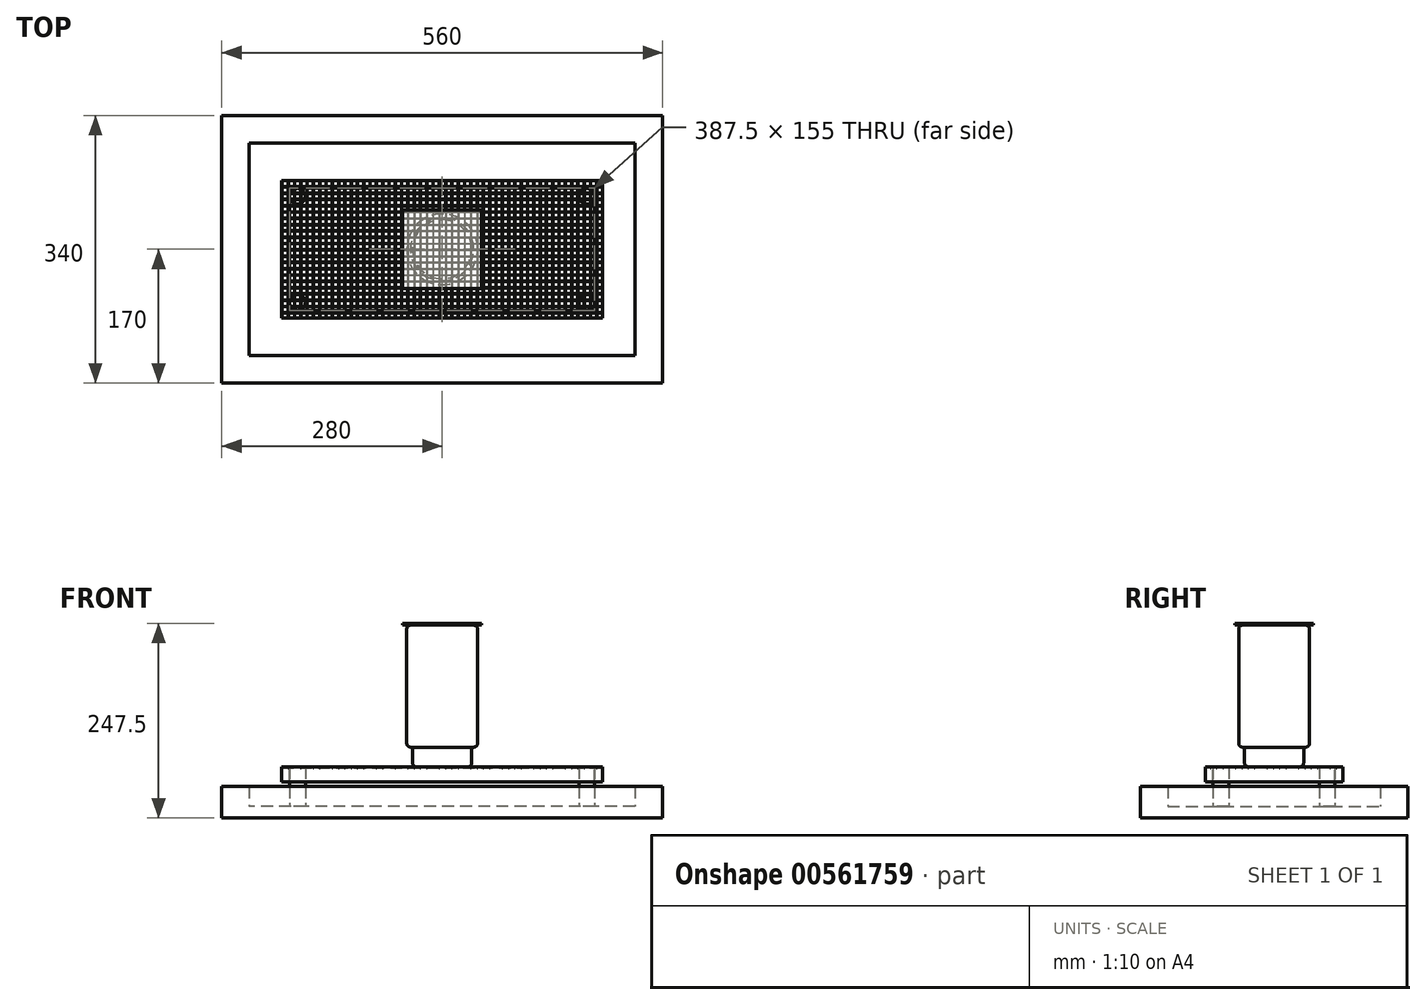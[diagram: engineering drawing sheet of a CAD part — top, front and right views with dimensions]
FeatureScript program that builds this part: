
annotation { "Feature Type Name" : "Feature", "Feature Type Description" : "" }
export const myFeature = defineFeature(function(context is Context, id is Id, definition is map)
    precondition{}
    {
        {
            var Q0;
            Q0=qCreatedBy(makeId("Top.planeOp"),FACE);
            cPlane(context, id + "F0", {"entities" : qUnion([Q0]), "cplaneType" : CPlaneType.OFFSET, "offset" : 167.5 * mm, "oppositeDirection" : true, "width" : 150 * mm, "height" : 150 * mm});
        }
        {
            var Q0;
            Q0=qCreatedBy(id+"F0.planeOp",FACE);
            var sketch = newSketch(context, id + "F1", { "sketchPlane" : qUnion([Q0])});
            skLineSegment(sketch, "E0.bottom", {"start": v(280, -170) * mm, "end": v(-280, -170) * mm});
            skLineSegment(sketch, "E0.top", {"start": v(280, 170) * mm, "end": v(-280, 170) * mm});
            skLineSegment(sketch, "E0.left", {"start": v(280, -170) * mm, "end": v(280, 170) * mm});
            skLineSegment(sketch, "E0.right", {"start": v(-280, -170) * mm, "end": v(-280, 170) * mm});
            skPoint(sketch, "E0.middle", {"position": v(0, 0) * mm});
            skSolve(sketch);
        }
        {
            var Q0;
            Q0=makeQuery(id+"F1.imprint","IMPRINT",FACE,{"disambiguationData":[TD([[makeQuery(id+"F1.imprint","IMPRINT",EDGE,{"derivedFrom":sQuery(id+"F1.wireOp",EDGE,"E0.bottom")}),-1.0]])]});
            extrude(context, id + "F2", {"entities" : qUnion([Q0]), "depth" : 40 * mm, "offsetDistance" : 25 * mm});
        }
        {
            var Q0;
            Q0=makeQuery(id+"F2.opExtrude","CAP_FACE",FACE,{"disambiguationData":[OSD([sQuery(id+"F1.wireOp",EDGE,"E0.bottom"),sQuery(id+"F1.wireOp",EDGE,"E0.top"),sQuery(id+"F1.wireOp",EDGE,"E0.left"),sQuery(id+"F1.wireOp",EDGE,"E0.right")])],"isStart":false});
            shell(context, id + "F3", {"entities" : qUnion([Q0]), "thickness" : 35 * mm});
        }
        {
            var Q0;
            Q0=makeQuery(id+"F3.opShell","OFFSET_FACE",FACE,{"disambiguationData":[OSD([sQuery(id+"F1.wireOp",EDGE,"E0.bottom"),sQuery(id+"F1.wireOp",EDGE,"E0.top"),sQuery(id+"F1.wireOp",EDGE,"E0.left"),sQuery(id+"F1.wireOp",EDGE,"E0.right")])]});
            var sketch = newSketch(context, id + "F4", { "sketchPlane" : qUnion([Q0])});
            skLineSegment(sketch, "E1.bottom", {"start": v(245, 135) * mm, "end": v(-245, 135) * mm});
            skLineSegment(sketch, "E1.top", {"start": v(245, -135) * mm, "end": v(-245, -135) * mm});
            skLineSegment(sketch, "E1.left", {"start": v(245, 135) * mm, "end": v(245, -135) * mm});
            skLineSegment(sketch, "E1.right", {"start": v(-245, 135) * mm, "end": v(-245, -135) * mm});
            skPoint(sketch, "E1.middle", {"position": v(0, 0) * mm});
            skSolve(sketch);
        }
        {
            var Q0;
            Q0=makeQuery(id+"F4.imprint","IMPRINT",FACE,{"disambiguationData":[TD([[makeQuery(id+"F4.imprint","IMPRINT",EDGE,{"derivedFrom":sQuery(id+"F4.wireOp",EDGE,"E1.bottom")}),1.0]])]});
            extrude(context, id + "F5", {"entities" : qUnion([Q0]), "operationType" : NewBodyOperationType.REMOVE, "oppositeDirection" : true, "depth" : 20 * mm, "offsetDistance" : 25 * mm});
        }
        {
            var Q0;
            Q0=makeQuery(id+"F5.boolean.opBoolean","COPY",FACE,{"derivedFrom":makeQuery(id+"F5.opExtrude","CAP_FACE",FACE,{"disambiguationData":[OSD([sQuery(id+"F4.wireOp",EDGE,"E1.bottom"),sQuery(id+"F4.wireOp",EDGE,"E1.top"),sQuery(id+"F4.wireOp",EDGE,"E1.left"),sQuery(id+"F4.wireOp",EDGE,"E1.right")])],"isStart":false})});
            var sketch = newSketch(context, id + "F6", { "sketchPlane" : qUnion([Q0])});
            skCircle(sketch, "E2", {"center": v(-183.75, 67.5) * mm, "radius": 10 * mm});
            skCircle(sketch, "E3", {"center": v(-183.75, -67.5) * mm, "radius": 10 * mm});
            skCircle(sketch, "E4", {"center": v(183.75, -67.5) * mm, "radius": 10 * mm});
            skCircle(sketch, "E5", {"center": v(183.75, 67.5) * mm, "radius": 10 * mm});
            skSolve(sketch);
        }
        {
            var Q0;
            Q0=makeQuery(id+"F6.imprint","IMPRINT",FACE,{"disambiguationData":[TD([[makeQuery(id+"F6.imprint","IMPRINT",EDGE,{"derivedFrom":sQuery(id+"F6.wireOp",EDGE,"E2")}),1.0]])]});
            var Q1;
            Q1=makeQuery(id+"F6.imprint","IMPRINT",FACE,{"disambiguationData":[TD([[makeQuery(id+"F6.imprint","IMPRINT",EDGE,{"derivedFrom":sQuery(id+"F6.wireOp",EDGE,"E5")}),1.0]])]});
            var Q2;
            Q2=makeQuery(id+"F6.imprint","IMPRINT",FACE,{"disambiguationData":[TD([[makeQuery(id+"F6.imprint","IMPRINT",EDGE,{"derivedFrom":sQuery(id+"F6.wireOp",EDGE,"E3")}),1.0]])]});
            var Q3;
            Q3=makeQuery(id+"F6.imprint","IMPRINT",FACE,{"disambiguationData":[TD([[makeQuery(id+"F6.imprint","IMPRINT",EDGE,{"derivedFrom":sQuery(id+"F6.wireOp",EDGE,"E4")}),1.0]])]});
            extrude(context, id + "F7", {"entities" : qUnion([Q0, Q1, Q2, Q3]), "operationType" : NewBodyOperationType.ADD, "depth" : 50 * mm, "offsetDistance" : 25 * mm});
        }
        {
            var Q0;
            Q0=makeQuery(id+"F7.opExtrude","CAP_FACE",FACE,{"disambiguationData":[OSD([sQuery(id+"F6.wireOp",EDGE,"E2")])],"isStart":false});
            var sketch = newSketch(context, id + "F8", { "sketchPlane" : qUnion([Q0])});
            skLineSegment(sketch, "E6.bottom", {"start": v(-183.75, 67.5) * mm, "end": v(183.75, 67.5) * mm});
            skLineSegment(sketch, "E6.top", {"start": v(-183.75, -67.5) * mm, "end": v(183.75, -67.5) * mm});
            skLineSegment(sketch, "E6.left", {"start": v(-183.75, 67.5) * mm, "end": v(-183.75, -67.5) * mm});
            skLineSegment(sketch, "E6.right", {"start": v(183.75, 67.5) * mm, "end": v(183.75, -67.5) * mm});
            skPoint(sketch, "E6.middle", {"position": v(0, 0) * mm});
            skLineSegment(sketch, "E7.bottom", {"start": v(193.75, 77.5) * mm, "end": v(-193.75, 77.5) * mm});
            skLineSegment(sketch, "E7.top", {"start": v(193.75, -77.5) * mm, "end": v(-193.75, -77.5) * mm});
            skLineSegment(sketch, "E7.left", {"start": v(193.75, 77.5) * mm, "end": v(193.75, -77.5) * mm});
            skLineSegment(sketch, "E7.right", {"start": v(-193.75, 77.5) * mm, "end": v(-193.75, -77.5) * mm});
            skLineSegment(sketch, "E8.bottom", {"start": v(203.75, 87.5) * mm, "end": v(-203.75, 87.5) * mm});
            skLineSegment(sketch, "E8.top", {"start": v(203.75, -87.5) * mm, "end": v(-203.75, -87.5) * mm});
            skLineSegment(sketch, "E8.left", {"start": v(203.75, 87.5) * mm, "end": v(203.75, -87.5) * mm});
            skLineSegment(sketch, "E8.right", {"start": v(-203.75, 87.5) * mm, "end": v(-203.75, -87.5) * mm});
            skSolve(sketch);
        }
        {
            var Q0;
            {var subQ1=sQuery(id+"F8.wireOp",EDGE,"E7.top");Q0=makeQuery(id+"F8.imprint","IMPRINT",FACE,{"disambiguationData":[TD([[makeQuery(id+"F8.imprint","IMPRINT",EDGE,{"derivedFrom":subQ1}),1.0]])]});}
            extrude(context, id + "F9", {"entities" : qUnion([Q0]), "operationType" : NewBodyOperationType.ADD, "oppositeDirection" : true, "depth" : 19.05 * mm, "offsetDistance" : 25 * mm});
        }
        {
            var Q0;
            Q0=makeQuery(id+"F9.opExtrude","CAP_FACE",FACE,{"disambiguationData":[OSD([sQuery(id+"F8.wireOp",EDGE,"E7.bottom"),sQuery(id+"F8.wireOp",EDGE,"E7.top"),sQuery(id+"F8.wireOp",EDGE,"E7.left"),sQuery(id+"F8.wireOp",EDGE,"E7.right"),sQuery(id+"F8.wireOp",EDGE,"E8.bottom"),sQuery(id+"F8.wireOp",EDGE,"E8.top"),sQuery(id+"F8.wireOp",EDGE,"E8.left"),sQuery(id+"F8.wireOp",EDGE,"E8.right")])],"isStart":true});
            var sketch = newSketch(context, id + "F10", { "sketchPlane" : qUnion([Q0])});
            skLineSegment(sketch, "E9.bottom", {"start": v(-203.75, 87.5) * mm, "end": v(203.75, 87.5) * mm});
            skLineSegment(sketch, "E9.top", {"start": v(-203.75, 87) * mm, "end": v(203.75, 87) * mm});
            skLineSegment(sketch, "E9.left", {"start": v(-203.75, 87.5) * mm, "end": v(-203.75, 87) * mm});
            skLineSegment(sketch, "E9.right", {"start": v(203.75, 87.5) * mm, "end": v(203.75, 87) * mm});
            skLineSegment(sketch, "E10.0.1.0", {"start": v(-203.75, 79.5) * mm, "end": v(-203.75, 79) * mm});
            skLineSegment(sketch, "E10.0.1.1", {"start": v(-203.75, 79) * mm, "end": v(203.75, 79) * mm});
            skLineSegment(sketch, "E10.0.1.2", {"start": v(-203.75, 79.5) * mm, "end": v(203.75, 79.5) * mm});
            skLineSegment(sketch, "E10.0.1.3", {"start": v(203.75, 79.5) * mm, "end": v(203.75, 79) * mm});
            skLineSegment(sketch, "E10.0.2.0", {"start": v(-203.75, 71.5) * mm, "end": v(-203.75, 71) * mm});
            skLineSegment(sketch, "E10.0.2.1", {"start": v(-203.75, 71) * mm, "end": v(203.75, 71) * mm});
            skLineSegment(sketch, "E10.0.2.2", {"start": v(-203.75, 71.5) * mm, "end": v(203.75, 71.5) * mm});
            skLineSegment(sketch, "E10.0.2.3", {"start": v(203.75, 71.5) * mm, "end": v(203.75, 71) * mm});
            skLineSegment(sketch, "E10.0.3.0", {"start": v(-203.75, 63.5) * mm, "end": v(-203.75, 63) * mm});
            skLineSegment(sketch, "E10.0.3.1", {"start": v(-203.75, 63) * mm, "end": v(203.75, 63) * mm});
            skLineSegment(sketch, "E10.0.3.2", {"start": v(-203.75, 63.5) * mm, "end": v(203.75, 63.5) * mm});
            skLineSegment(sketch, "E10.0.3.3", {"start": v(203.75, 63.5) * mm, "end": v(203.75, 63) * mm});
            skLineSegment(sketch, "E10.0.4.0", {"start": v(-203.75, 55.5) * mm, "end": v(-203.75, 55) * mm});
            skLineSegment(sketch, "E10.0.4.1", {"start": v(-203.75, 55) * mm, "end": v(203.75, 55) * mm});
            skLineSegment(sketch, "E10.0.4.2", {"start": v(-203.75, 55.5) * mm, "end": v(203.75, 55.5) * mm});
            skLineSegment(sketch, "E10.0.4.3", {"start": v(203.75, 55.5) * mm, "end": v(203.75, 55) * mm});
            skLineSegment(sketch, "E10.0.5.0", {"start": v(-203.75, 47.5) * mm, "end": v(-203.75, 47) * mm});
            skLineSegment(sketch, "E10.0.5.1", {"start": v(-203.75, 47) * mm, "end": v(203.75, 47) * mm});
            skLineSegment(sketch, "E10.0.5.2", {"start": v(-203.75, 47.5) * mm, "end": v(203.75, 47.5) * mm});
            skLineSegment(sketch, "E10.0.5.3", {"start": v(203.75, 47.5) * mm, "end": v(203.75, 47) * mm});
            skLineSegment(sketch, "E10.0.6.0", {"start": v(-203.75, 39.5) * mm, "end": v(-203.75, 39) * mm});
            skLineSegment(sketch, "E10.0.6.1", {"start": v(-203.75, 39) * mm, "end": v(203.75, 39) * mm});
            skLineSegment(sketch, "E10.0.6.2", {"start": v(-203.75, 39.5) * mm, "end": v(203.75, 39.5) * mm});
            skLineSegment(sketch, "E10.0.6.3", {"start": v(203.75, 39.5) * mm, "end": v(203.75, 39) * mm});
            skLineSegment(sketch, "E10.0.7.0", {"start": v(-203.75, 31.5) * mm, "end": v(-203.75, 31) * mm});
            skLineSegment(sketch, "E10.0.7.1", {"start": v(-203.75, 31) * mm, "end": v(203.75, 31) * mm});
            skLineSegment(sketch, "E10.0.7.2", {"start": v(-203.75, 31.5) * mm, "end": v(203.75, 31.5) * mm});
            skLineSegment(sketch, "E10.0.7.3", {"start": v(203.75, 31.5) * mm, "end": v(203.75, 31) * mm});
            skLineSegment(sketch, "E10.0.8.0", {"start": v(-203.75, 23.5) * mm, "end": v(-203.75, 23) * mm});
            skLineSegment(sketch, "E10.0.8.1", {"start": v(-203.75, 23) * mm, "end": v(203.75, 23) * mm});
            skLineSegment(sketch, "E10.0.8.2", {"start": v(-203.75, 23.5) * mm, "end": v(203.75, 23.5) * mm});
            skLineSegment(sketch, "E10.0.8.3", {"start": v(203.75, 23.5) * mm, "end": v(203.75, 23) * mm});
            skLineSegment(sketch, "E10.0.9.0", {"start": v(-203.75, 15.5) * mm, "end": v(-203.75, 15) * mm});
            skLineSegment(sketch, "E10.0.9.1", {"start": v(-203.75, 15) * mm, "end": v(203.75, 15) * mm});
            skLineSegment(sketch, "E10.0.9.2", {"start": v(-203.75, 15.5) * mm, "end": v(203.75, 15.5) * mm});
            skLineSegment(sketch, "E10.0.9.3", {"start": v(203.75, 15.5) * mm, "end": v(203.75, 15) * mm});
            skLineSegment(sketch, "E10.0.10.0", {"start": v(-203.75, 7.5) * mm, "end": v(-203.75, 7) * mm});
            skLineSegment(sketch, "E10.0.10.1", {"start": v(-203.75, 7) * mm, "end": v(203.75, 7) * mm});
            skLineSegment(sketch, "E10.0.10.2", {"start": v(-203.75, 7.5) * mm, "end": v(203.75, 7.5) * mm});
            skLineSegment(sketch, "E10.0.10.3", {"start": v(203.75, 7.5) * mm, "end": v(203.75, 7) * mm});
            skLineSegment(sketch, "E10.0.11.0", {"start": v(-203.75, -0.5) * mm, "end": v(-203.75, -1) * mm});
            skLineSegment(sketch, "E10.0.11.1", {"start": v(-203.75, -1) * mm, "end": v(203.75, -1) * mm});
            skLineSegment(sketch, "E10.0.11.2", {"start": v(-203.75, -0.5) * mm, "end": v(203.75, -0.5) * mm});
            skLineSegment(sketch, "E10.0.11.3", {"start": v(203.75, -0.5) * mm, "end": v(203.75, -1) * mm});
            skLineSegment(sketch, "E10.0.12.0", {"start": v(-203.75, -8.5) * mm, "end": v(-203.75, -9) * mm});
            skLineSegment(sketch, "E10.0.12.1", {"start": v(-203.75, -9) * mm, "end": v(203.75, -9) * mm});
            skLineSegment(sketch, "E10.0.12.2", {"start": v(-203.75, -8.5) * mm, "end": v(203.75, -8.5) * mm});
            skLineSegment(sketch, "E10.0.12.3", {"start": v(203.75, -8.5) * mm, "end": v(203.75, -9) * mm});
            skLineSegment(sketch, "E10.0.13.0", {"start": v(-203.75, -16.5) * mm, "end": v(-203.75, -17) * mm});
            skLineSegment(sketch, "E10.0.13.1", {"start": v(-203.75, -17) * mm, "end": v(203.75, -17) * mm});
            skLineSegment(sketch, "E10.0.13.2", {"start": v(-203.75, -16.5) * mm, "end": v(203.75, -16.5) * mm});
            skLineSegment(sketch, "E10.0.13.3", {"start": v(203.75, -16.5) * mm, "end": v(203.75, -17) * mm});
            skLineSegment(sketch, "E10.0.14.0", {"start": v(-203.75, -24.5) * mm, "end": v(-203.75, -25) * mm});
            skLineSegment(sketch, "E10.0.14.1", {"start": v(-203.75, -25) * mm, "end": v(203.75, -25) * mm});
            skLineSegment(sketch, "E10.0.14.2", {"start": v(-203.75, -24.5) * mm, "end": v(203.75, -24.5) * mm});
            skLineSegment(sketch, "E10.0.14.3", {"start": v(203.75, -24.5) * mm, "end": v(203.75, -25) * mm});
            skLineSegment(sketch, "E10.0.15.0", {"start": v(-203.75, -32.5) * mm, "end": v(-203.75, -33) * mm});
            skLineSegment(sketch, "E10.0.15.1", {"start": v(-203.75, -33) * mm, "end": v(203.75, -33) * mm});
            skLineSegment(sketch, "E10.0.15.2", {"start": v(-203.75, -32.5) * mm, "end": v(203.75, -32.5) * mm});
            skLineSegment(sketch, "E10.0.15.3", {"start": v(203.75, -32.5) * mm, "end": v(203.75, -33) * mm});
            skLineSegment(sketch, "E10.0.16.0", {"start": v(-203.75, -40.5) * mm, "end": v(-203.75, -41) * mm});
            skLineSegment(sketch, "E10.0.16.1", {"start": v(-203.75, -41) * mm, "end": v(203.75, -41) * mm});
            skLineSegment(sketch, "E10.0.16.2", {"start": v(-203.75, -40.5) * mm, "end": v(203.75, -40.5) * mm});
            skLineSegment(sketch, "E10.0.16.3", {"start": v(203.75, -40.5) * mm, "end": v(203.75, -41) * mm});
            skLineSegment(sketch, "E10.0.17.0", {"start": v(-203.75, -48.5) * mm, "end": v(-203.75, -49) * mm});
            skLineSegment(sketch, "E10.0.17.1", {"start": v(-203.75, -49) * mm, "end": v(203.75, -49) * mm});
            skLineSegment(sketch, "E10.0.17.2", {"start": v(-203.75, -48.5) * mm, "end": v(203.75, -48.5) * mm});
            skLineSegment(sketch, "E10.0.17.3", {"start": v(203.75, -48.5) * mm, "end": v(203.75, -49) * mm});
            skLineSegment(sketch, "E10.0.18.0", {"start": v(-203.75, -56.5) * mm, "end": v(-203.75, -57) * mm});
            skLineSegment(sketch, "E10.0.18.1", {"start": v(-203.75, -57) * mm, "end": v(203.75, -57) * mm});
            skLineSegment(sketch, "E10.0.18.2", {"start": v(-203.75, -56.5) * mm, "end": v(203.75, -56.5) * mm});
            skLineSegment(sketch, "E10.0.18.3", {"start": v(203.75, -56.5) * mm, "end": v(203.75, -57) * mm});
            skLineSegment(sketch, "E10.0.19.0", {"start": v(-203.75, -64.5) * mm, "end": v(-203.75, -65) * mm});
            skLineSegment(sketch, "E10.0.19.1", {"start": v(-203.75, -65) * mm, "end": v(203.75, -65) * mm});
            skLineSegment(sketch, "E10.0.19.2", {"start": v(-203.75, -64.5) * mm, "end": v(203.75, -64.5) * mm});
            skLineSegment(sketch, "E10.0.19.3", {"start": v(203.75, -64.5) * mm, "end": v(203.75, -65) * mm});
            skLineSegment(sketch, "E10.0.20.0", {"start": v(-203.75, -72.5) * mm, "end": v(-203.75, -73) * mm});
            skLineSegment(sketch, "E10.0.20.1", {"start": v(-203.75, -73) * mm, "end": v(203.75, -73) * mm});
            skLineSegment(sketch, "E10.0.20.2", {"start": v(-203.75, -72.5) * mm, "end": v(203.75, -72.5) * mm});
            skLineSegment(sketch, "E10.0.20.3", {"start": v(203.75, -72.5) * mm, "end": v(203.75, -73) * mm});
            skLineSegment(sketch, "E10.0.21.0", {"start": v(-203.75, -80.5) * mm, "end": v(-203.75, -81) * mm});
            skLineSegment(sketch, "E10.0.21.1", {"start": v(-203.75, -81) * mm, "end": v(203.75, -81) * mm});
            skLineSegment(sketch, "E10.0.21.2", {"start": v(-203.75, -80.5) * mm, "end": v(203.75, -80.5) * mm});
            skLineSegment(sketch, "E10.0.21.3", {"start": v(203.75, -80.5) * mm, "end": v(203.75, -81) * mm});
            skLineSegment(sketch, "E10.direction1", {"start": v(-203.75, 87) * mm, "end": v(-178.75, 87) * mm, "construction": true});
            skLineSegment(sketch, "E10.direction2", {"start": v(-203.75, 87) * mm, "end": v(-203.75, 79) * mm, "construction": true});
            skSolve(sketch);
        }
        {
            var Q0;
            Q0 = qSketchRegion(id + "F10", true);
            extrude(context, id + "F11", {"entities" : qUnion([Q0]), "oppositeDirection" : true, "depth" : 1 * mm, "offsetDistance" : 25 * mm});
        }
        {
            var Q0;
            Q0=makeQuery(id+"F9.opExtrude","CAP_FACE",FACE,{"disambiguationData":[OSD([sQuery(id+"F8.wireOp",EDGE,"E7.bottom"),sQuery(id+"F8.wireOp",EDGE,"E7.top"),sQuery(id+"F8.wireOp",EDGE,"E7.left"),sQuery(id+"F8.wireOp",EDGE,"E7.right"),sQuery(id+"F8.wireOp",EDGE,"E8.bottom"),sQuery(id+"F8.wireOp",EDGE,"E8.top"),sQuery(id+"F8.wireOp",EDGE,"E8.left"),sQuery(id+"F8.wireOp",EDGE,"E8.right")])],"isStart":true});
            var sketch = newSketch(context, id + "F12", { "sketchPlane" : qUnion([Q0])});
            skLineSegment(sketch, "E11.bottom", {"start": v(-203.75, 87.5) * mm, "end": v(-203.25, 87.5) * mm});
            skLineSegment(sketch, "E11.top", {"start": v(-203.75, -87.5) * mm, "end": v(-203.25, -87.5) * mm});
            skLineSegment(sketch, "E11.left", {"start": v(-203.75, 87.5) * mm, "end": v(-203.75, -87.5) * mm});
            skLineSegment(sketch, "E11.right", {"start": v(-203.25, 87.5) * mm, "end": v(-203.25, -87.5) * mm});
            skLineSegment(sketch, "E12.1.0.0", {"start": v(-195.75, 87.5) * mm, "end": v(-195.75, -87.5) * mm});
            skLineSegment(sketch, "E12.1.0.1", {"start": v(-195.25, 87.5) * mm, "end": v(-195.25, -87.5) * mm});
            skLineSegment(sketch, "E12.1.0.2", {"start": v(-195.75, -87.5) * mm, "end": v(-195.25, -87.5) * mm});
            skLineSegment(sketch, "E12.1.0.3", {"start": v(-195.75, 87.5) * mm, "end": v(-195.25, 87.5) * mm});
            skLineSegment(sketch, "E12.2.0.0", {"start": v(-187.75, 87.5) * mm, "end": v(-187.75, -87.5) * mm});
            skLineSegment(sketch, "E12.2.0.1", {"start": v(-187.25, 87.5) * mm, "end": v(-187.25, -87.5) * mm});
            skLineSegment(sketch, "E12.2.0.2", {"start": v(-187.75, -87.5) * mm, "end": v(-187.25, -87.5) * mm});
            skLineSegment(sketch, "E12.2.0.3", {"start": v(-187.75, 87.5) * mm, "end": v(-187.25, 87.5) * mm});
            skLineSegment(sketch, "E12.3.0.0", {"start": v(-179.75, 87.5) * mm, "end": v(-179.75, -87.5) * mm});
            skLineSegment(sketch, "E12.3.0.1", {"start": v(-179.25, 87.5) * mm, "end": v(-179.25, -87.5) * mm});
            skLineSegment(sketch, "E12.3.0.2", {"start": v(-179.75, -87.5) * mm, "end": v(-179.25, -87.5) * mm});
            skLineSegment(sketch, "E12.3.0.3", {"start": v(-179.75, 87.5) * mm, "end": v(-179.25, 87.5) * mm});
            skLineSegment(sketch, "E12.4.0.0", {"start": v(-171.75, 87.5) * mm, "end": v(-171.75, -87.5) * mm});
            skLineSegment(sketch, "E12.4.0.1", {"start": v(-171.25, 87.5) * mm, "end": v(-171.25, -87.5) * mm});
            skLineSegment(sketch, "E12.4.0.2", {"start": v(-171.75, -87.5) * mm, "end": v(-171.25, -87.5) * mm});
            skLineSegment(sketch, "E12.4.0.3", {"start": v(-171.75, 87.5) * mm, "end": v(-171.25, 87.5) * mm});
            skLineSegment(sketch, "E12.5.0.0", {"start": v(-163.75, 87.5) * mm, "end": v(-163.75, -87.5) * mm});
            skLineSegment(sketch, "E12.5.0.1", {"start": v(-163.25, 87.5) * mm, "end": v(-163.25, -87.5) * mm});
            skLineSegment(sketch, "E12.5.0.2", {"start": v(-163.75, -87.5) * mm, "end": v(-163.25, -87.5) * mm});
            skLineSegment(sketch, "E12.5.0.3", {"start": v(-163.75, 87.5) * mm, "end": v(-163.25, 87.5) * mm});
            skLineSegment(sketch, "E12.6.0.0", {"start": v(-155.75, 87.5) * mm, "end": v(-155.75, -87.5) * mm});
            skLineSegment(sketch, "E12.6.0.1", {"start": v(-155.25, 87.5) * mm, "end": v(-155.25, -87.5) * mm});
            skLineSegment(sketch, "E12.6.0.2", {"start": v(-155.75, -87.5) * mm, "end": v(-155.25, -87.5) * mm});
            skLineSegment(sketch, "E12.6.0.3", {"start": v(-155.75, 87.5) * mm, "end": v(-155.25, 87.5) * mm});
            skLineSegment(sketch, "E12.7.0.0", {"start": v(-147.75, 87.5) * mm, "end": v(-147.75, -87.5) * mm});
            skLineSegment(sketch, "E12.7.0.1", {"start": v(-147.25, 87.5) * mm, "end": v(-147.25, -87.5) * mm});
            skLineSegment(sketch, "E12.7.0.2", {"start": v(-147.75, -87.5) * mm, "end": v(-147.25, -87.5) * mm});
            skLineSegment(sketch, "E12.7.0.3", {"start": v(-147.75, 87.5) * mm, "end": v(-147.25, 87.5) * mm});
            skLineSegment(sketch, "E12.8.0.0", {"start": v(-139.75, 87.5) * mm, "end": v(-139.75, -87.5) * mm});
            skLineSegment(sketch, "E12.8.0.1", {"start": v(-139.25, 87.5) * mm, "end": v(-139.25, -87.5) * mm});
            skLineSegment(sketch, "E12.8.0.2", {"start": v(-139.75, -87.5) * mm, "end": v(-139.25, -87.5) * mm});
            skLineSegment(sketch, "E12.8.0.3", {"start": v(-139.75, 87.5) * mm, "end": v(-139.25, 87.5) * mm});
            skLineSegment(sketch, "E12.9.0.0", {"start": v(-131.75, 87.5) * mm, "end": v(-131.75, -87.5) * mm});
            skLineSegment(sketch, "E12.9.0.1", {"start": v(-131.25, 87.5) * mm, "end": v(-131.25, -87.5) * mm});
            skLineSegment(sketch, "E12.9.0.2", {"start": v(-131.75, -87.5) * mm, "end": v(-131.25, -87.5) * mm});
            skLineSegment(sketch, "E12.9.0.3", {"start": v(-131.75, 87.5) * mm, "end": v(-131.25, 87.5) * mm});
            skLineSegment(sketch, "E12.10.0.0", {"start": v(-123.75, 87.5) * mm, "end": v(-123.75, -87.5) * mm});
            skLineSegment(sketch, "E12.10.0.1", {"start": v(-123.25, 87.5) * mm, "end": v(-123.25, -87.5) * mm});
            skLineSegment(sketch, "E12.10.0.2", {"start": v(-123.75, -87.5) * mm, "end": v(-123.25, -87.5) * mm});
            skLineSegment(sketch, "E12.10.0.3", {"start": v(-123.75, 87.5) * mm, "end": v(-123.25, 87.5) * mm});
            skLineSegment(sketch, "E12.11.0.0", {"start": v(-115.75, 87.5) * mm, "end": v(-115.75, -87.5) * mm});
            skLineSegment(sketch, "E12.11.0.1", {"start": v(-115.25, 87.5) * mm, "end": v(-115.25, -87.5) * mm});
            skLineSegment(sketch, "E12.11.0.2", {"start": v(-115.75, -87.5) * mm, "end": v(-115.25, -87.5) * mm});
            skLineSegment(sketch, "E12.11.0.3", {"start": v(-115.75, 87.5) * mm, "end": v(-115.25, 87.5) * mm});
            skLineSegment(sketch, "E12.12.0.0", {"start": v(-107.75, 87.5) * mm, "end": v(-107.75, -87.5) * mm});
            skLineSegment(sketch, "E12.12.0.1", {"start": v(-107.25, 87.5) * mm, "end": v(-107.25, -87.5) * mm});
            skLineSegment(sketch, "E12.12.0.2", {"start": v(-107.75, -87.5) * mm, "end": v(-107.25, -87.5) * mm});
            skLineSegment(sketch, "E12.12.0.3", {"start": v(-107.75, 87.5) * mm, "end": v(-107.25, 87.5) * mm});
            skLineSegment(sketch, "E12.13.0.0", {"start": v(-99.75, 87.5) * mm, "end": v(-99.75, -87.5) * mm});
            skLineSegment(sketch, "E12.13.0.1", {"start": v(-99.25, 87.5) * mm, "end": v(-99.25, -87.5) * mm});
            skLineSegment(sketch, "E12.13.0.2", {"start": v(-99.75, -87.5) * mm, "end": v(-99.25, -87.5) * mm});
            skLineSegment(sketch, "E12.13.0.3", {"start": v(-99.75, 87.5) * mm, "end": v(-99.25, 87.5) * mm});
            skLineSegment(sketch, "E12.14.0.0", {"start": v(-91.75, 87.5) * mm, "end": v(-91.75, -87.5) * mm});
            skLineSegment(sketch, "E12.14.0.1", {"start": v(-91.25, 87.5) * mm, "end": v(-91.25, -87.5) * mm});
            skLineSegment(sketch, "E12.14.0.2", {"start": v(-91.75, -87.5) * mm, "end": v(-91.25, -87.5) * mm});
            skLineSegment(sketch, "E12.14.0.3", {"start": v(-91.75, 87.5) * mm, "end": v(-91.25, 87.5) * mm});
            skLineSegment(sketch, "E12.15.0.0", {"start": v(-83.75, 87.5) * mm, "end": v(-83.75, -87.5) * mm});
            skLineSegment(sketch, "E12.15.0.1", {"start": v(-83.25, 87.5) * mm, "end": v(-83.25, -87.5) * mm});
            skLineSegment(sketch, "E12.15.0.2", {"start": v(-83.75, -87.5) * mm, "end": v(-83.25, -87.5) * mm});
            skLineSegment(sketch, "E12.15.0.3", {"start": v(-83.75, 87.5) * mm, "end": v(-83.25, 87.5) * mm});
            skLineSegment(sketch, "E12.16.0.0", {"start": v(-75.75, 87.5) * mm, "end": v(-75.75, -87.5) * mm});
            skLineSegment(sketch, "E12.16.0.1", {"start": v(-75.25, 87.5) * mm, "end": v(-75.25, -87.5) * mm});
            skLineSegment(sketch, "E12.16.0.2", {"start": v(-75.75, -87.5) * mm, "end": v(-75.25, -87.5) * mm});
            skLineSegment(sketch, "E12.16.0.3", {"start": v(-75.75, 87.5) * mm, "end": v(-75.25, 87.5) * mm});
            skLineSegment(sketch, "E12.17.0.0", {"start": v(-67.75, 87.5) * mm, "end": v(-67.75, -87.5) * mm});
            skLineSegment(sketch, "E12.17.0.1", {"start": v(-67.25, 87.5) * mm, "end": v(-67.25, -87.5) * mm});
            skLineSegment(sketch, "E12.17.0.2", {"start": v(-67.75, -87.5) * mm, "end": v(-67.25, -87.5) * mm});
            skLineSegment(sketch, "E12.17.0.3", {"start": v(-67.75, 87.5) * mm, "end": v(-67.25, 87.5) * mm});
            skLineSegment(sketch, "E12.18.0.0", {"start": v(-59.75, 87.5) * mm, "end": v(-59.75, -87.5) * mm});
            skLineSegment(sketch, "E12.18.0.1", {"start": v(-59.25, 87.5) * mm, "end": v(-59.25, -87.5) * mm});
            skLineSegment(sketch, "E12.18.0.2", {"start": v(-59.75, -87.5) * mm, "end": v(-59.25, -87.5) * mm});
            skLineSegment(sketch, "E12.18.0.3", {"start": v(-59.75, 87.5) * mm, "end": v(-59.25, 87.5) * mm});
            skLineSegment(sketch, "E12.19.0.0", {"start": v(-51.75, 87.5) * mm, "end": v(-51.75, -87.5) * mm});
            skLineSegment(sketch, "E12.19.0.1", {"start": v(-51.25, 87.5) * mm, "end": v(-51.25, -87.5) * mm});
            skLineSegment(sketch, "E12.19.0.2", {"start": v(-51.75, -87.5) * mm, "end": v(-51.25, -87.5) * mm});
            skLineSegment(sketch, "E12.19.0.3", {"start": v(-51.75, 87.5) * mm, "end": v(-51.25, 87.5) * mm});
            skLineSegment(sketch, "E12.20.0.0", {"start": v(-43.75, 87.5) * mm, "end": v(-43.75, -87.5) * mm});
            skLineSegment(sketch, "E12.20.0.1", {"start": v(-43.25, 87.5) * mm, "end": v(-43.25, -87.5) * mm});
            skLineSegment(sketch, "E12.20.0.2", {"start": v(-43.75, -87.5) * mm, "end": v(-43.25, -87.5) * mm});
            skLineSegment(sketch, "E12.20.0.3", {"start": v(-43.75, 87.5) * mm, "end": v(-43.25, 87.5) * mm});
            skLineSegment(sketch, "E12.21.0.0", {"start": v(-35.75, 87.5) * mm, "end": v(-35.75, -87.5) * mm});
            skLineSegment(sketch, "E12.21.0.1", {"start": v(-35.25, 87.5) * mm, "end": v(-35.25, -87.5) * mm});
            skLineSegment(sketch, "E12.21.0.2", {"start": v(-35.75, -87.5) * mm, "end": v(-35.25, -87.5) * mm});
            skLineSegment(sketch, "E12.21.0.3", {"start": v(-35.75, 87.5) * mm, "end": v(-35.25, 87.5) * mm});
            skLineSegment(sketch, "E12.22.0.0", {"start": v(-27.75, 87.5) * mm, "end": v(-27.75, -87.5) * mm});
            skLineSegment(sketch, "E12.22.0.1", {"start": v(-27.25, 87.5) * mm, "end": v(-27.25, -87.5) * mm});
            skLineSegment(sketch, "E12.22.0.2", {"start": v(-27.75, -87.5) * mm, "end": v(-27.25, -87.5) * mm});
            skLineSegment(sketch, "E12.22.0.3", {"start": v(-27.75, 87.5) * mm, "end": v(-27.25, 87.5) * mm});
            skLineSegment(sketch, "E12.23.0.0", {"start": v(-19.75, 87.5) * mm, "end": v(-19.75, -87.5) * mm});
            skLineSegment(sketch, "E12.23.0.1", {"start": v(-19.25, 87.5) * mm, "end": v(-19.25, -87.5) * mm});
            skLineSegment(sketch, "E12.23.0.2", {"start": v(-19.75, -87.5) * mm, "end": v(-19.25, -87.5) * mm});
            skLineSegment(sketch, "E12.23.0.3", {"start": v(-19.75, 87.5) * mm, "end": v(-19.25, 87.5) * mm});
            skLineSegment(sketch, "E12.24.0.0", {"start": v(-11.75, 87.5) * mm, "end": v(-11.75, -87.5) * mm});
            skLineSegment(sketch, "E12.24.0.1", {"start": v(-11.25, 87.5) * mm, "end": v(-11.25, -87.5) * mm});
            skLineSegment(sketch, "E12.24.0.2", {"start": v(-11.75, -87.5) * mm, "end": v(-11.25, -87.5) * mm});
            skLineSegment(sketch, "E12.24.0.3", {"start": v(-11.75, 87.5) * mm, "end": v(-11.25, 87.5) * mm});
            skLineSegment(sketch, "E12.25.0.0", {"start": v(-3.75, 87.5) * mm, "end": v(-3.75, -87.5) * mm});
            skLineSegment(sketch, "E12.25.0.1", {"start": v(-3.25, 87.5) * mm, "end": v(-3.25, -87.5) * mm});
            skLineSegment(sketch, "E12.25.0.2", {"start": v(-3.75, -87.5) * mm, "end": v(-3.25, -87.5) * mm});
            skLineSegment(sketch, "E12.25.0.3", {"start": v(-3.75, 87.5) * mm, "end": v(-3.25, 87.5) * mm});
            skLineSegment(sketch, "E12.26.0.0", {"start": v(4.25, 87.5) * mm, "end": v(4.25, -87.5) * mm});
            skLineSegment(sketch, "E12.26.0.1", {"start": v(4.75, 87.5) * mm, "end": v(4.75, -87.5) * mm});
            skLineSegment(sketch, "E12.26.0.2", {"start": v(4.25, -87.5) * mm, "end": v(4.75, -87.5) * mm});
            skLineSegment(sketch, "E12.26.0.3", {"start": v(4.25, 87.5) * mm, "end": v(4.75, 87.5) * mm});
            skLineSegment(sketch, "E12.27.0.0", {"start": v(12.25, 87.5) * mm, "end": v(12.25, -87.5) * mm});
            skLineSegment(sketch, "E12.27.0.1", {"start": v(12.75, 87.5) * mm, "end": v(12.75, -87.5) * mm});
            skLineSegment(sketch, "E12.27.0.2", {"start": v(12.25, -87.5) * mm, "end": v(12.75, -87.5) * mm});
            skLineSegment(sketch, "E12.27.0.3", {"start": v(12.25, 87.5) * mm, "end": v(12.75, 87.5) * mm});
            skLineSegment(sketch, "E12.28.0.0", {"start": v(20.25, 87.5) * mm, "end": v(20.25, -87.5) * mm});
            skLineSegment(sketch, "E12.28.0.1", {"start": v(20.75, 87.5) * mm, "end": v(20.75, -87.5) * mm});
            skLineSegment(sketch, "E12.28.0.2", {"start": v(20.25, -87.5) * mm, "end": v(20.75, -87.5) * mm});
            skLineSegment(sketch, "E12.28.0.3", {"start": v(20.25, 87.5) * mm, "end": v(20.75, 87.5) * mm});
            skLineSegment(sketch, "E12.29.0.0", {"start": v(28.25, 87.5) * mm, "end": v(28.25, -87.5) * mm});
            skLineSegment(sketch, "E12.29.0.1", {"start": v(28.75, 87.5) * mm, "end": v(28.75, -87.5) * mm});
            skLineSegment(sketch, "E12.29.0.2", {"start": v(28.25, -87.5) * mm, "end": v(28.75, -87.5) * mm});
            skLineSegment(sketch, "E12.29.0.3", {"start": v(28.25, 87.5) * mm, "end": v(28.75, 87.5) * mm});
            skLineSegment(sketch, "E12.30.0.0", {"start": v(36.25, 87.5) * mm, "end": v(36.25, -87.5) * mm});
            skLineSegment(sketch, "E12.30.0.1", {"start": v(36.75, 87.5) * mm, "end": v(36.75, -87.5) * mm});
            skLineSegment(sketch, "E12.30.0.2", {"start": v(36.25, -87.5) * mm, "end": v(36.75, -87.5) * mm});
            skLineSegment(sketch, "E12.30.0.3", {"start": v(36.25, 87.5) * mm, "end": v(36.75, 87.5) * mm});
            skLineSegment(sketch, "E12.31.0.0", {"start": v(44.25, 87.5) * mm, "end": v(44.25, -87.5) * mm});
            skLineSegment(sketch, "E12.31.0.1", {"start": v(44.75, 87.5) * mm, "end": v(44.75, -87.5) * mm});
            skLineSegment(sketch, "E12.31.0.2", {"start": v(44.25, -87.5) * mm, "end": v(44.75, -87.5) * mm});
            skLineSegment(sketch, "E12.31.0.3", {"start": v(44.25, 87.5) * mm, "end": v(44.75, 87.5) * mm});
            skLineSegment(sketch, "E12.32.0.0", {"start": v(52.25, 87.5) * mm, "end": v(52.25, -87.5) * mm});
            skLineSegment(sketch, "E12.32.0.1", {"start": v(52.75, 87.5) * mm, "end": v(52.75, -87.5) * mm});
            skLineSegment(sketch, "E12.32.0.2", {"start": v(52.25, -87.5) * mm, "end": v(52.75, -87.5) * mm});
            skLineSegment(sketch, "E12.32.0.3", {"start": v(52.25, 87.5) * mm, "end": v(52.75, 87.5) * mm});
            skLineSegment(sketch, "E12.33.0.0", {"start": v(60.25, 87.5) * mm, "end": v(60.25, -87.5) * mm});
            skLineSegment(sketch, "E12.33.0.1", {"start": v(60.75, 87.5) * mm, "end": v(60.75, -87.5) * mm});
            skLineSegment(sketch, "E12.33.0.2", {"start": v(60.25, -87.5) * mm, "end": v(60.75, -87.5) * mm});
            skLineSegment(sketch, "E12.33.0.3", {"start": v(60.25, 87.5) * mm, "end": v(60.75, 87.5) * mm});
            skLineSegment(sketch, "E12.34.0.0", {"start": v(68.25, 87.5) * mm, "end": v(68.25, -87.5) * mm});
            skLineSegment(sketch, "E12.34.0.1", {"start": v(68.75, 87.5) * mm, "end": v(68.75, -87.5) * mm});
            skLineSegment(sketch, "E12.34.0.2", {"start": v(68.25, -87.5) * mm, "end": v(68.75, -87.5) * mm});
            skLineSegment(sketch, "E12.34.0.3", {"start": v(68.25, 87.5) * mm, "end": v(68.75, 87.5) * mm});
            skLineSegment(sketch, "E12.35.0.0", {"start": v(76.25, 87.5) * mm, "end": v(76.25, -87.5) * mm});
            skLineSegment(sketch, "E12.35.0.1", {"start": v(76.75, 87.5) * mm, "end": v(76.75, -87.5) * mm});
            skLineSegment(sketch, "E12.35.0.2", {"start": v(76.25, -87.5) * mm, "end": v(76.75, -87.5) * mm});
            skLineSegment(sketch, "E12.35.0.3", {"start": v(76.25, 87.5) * mm, "end": v(76.75, 87.5) * mm});
            skLineSegment(sketch, "E12.36.0.0", {"start": v(84.25, 87.5) * mm, "end": v(84.25, -87.5) * mm});
            skLineSegment(sketch, "E12.36.0.1", {"start": v(84.75, 87.5) * mm, "end": v(84.75, -87.5) * mm});
            skLineSegment(sketch, "E12.36.0.2", {"start": v(84.25, -87.5) * mm, "end": v(84.75, -87.5) * mm});
            skLineSegment(sketch, "E12.36.0.3", {"start": v(84.25, 87.5) * mm, "end": v(84.75, 87.5) * mm});
            skLineSegment(sketch, "E12.37.0.0", {"start": v(92.25, 87.5) * mm, "end": v(92.25, -87.5) * mm});
            skLineSegment(sketch, "E12.37.0.1", {"start": v(92.75, 87.5) * mm, "end": v(92.75, -87.5) * mm});
            skLineSegment(sketch, "E12.37.0.2", {"start": v(92.25, -87.5) * mm, "end": v(92.75, -87.5) * mm});
            skLineSegment(sketch, "E12.37.0.3", {"start": v(92.25, 87.5) * mm, "end": v(92.75, 87.5) * mm});
            skLineSegment(sketch, "E12.38.0.0", {"start": v(100.25, 87.5) * mm, "end": v(100.25, -87.5) * mm});
            skLineSegment(sketch, "E12.38.0.1", {"start": v(100.75, 87.5) * mm, "end": v(100.75, -87.5) * mm});
            skLineSegment(sketch, "E12.38.0.2", {"start": v(100.25, -87.5) * mm, "end": v(100.75, -87.5) * mm});
            skLineSegment(sketch, "E12.38.0.3", {"start": v(100.25, 87.5) * mm, "end": v(100.75, 87.5) * mm});
            skLineSegment(sketch, "E12.39.0.0", {"start": v(108.25, 87.5) * mm, "end": v(108.25, -87.5) * mm});
            skLineSegment(sketch, "E12.39.0.1", {"start": v(108.75, 87.5) * mm, "end": v(108.75, -87.5) * mm});
            skLineSegment(sketch, "E12.39.0.2", {"start": v(108.25, -87.5) * mm, "end": v(108.75, -87.5) * mm});
            skLineSegment(sketch, "E12.39.0.3", {"start": v(108.25, 87.5) * mm, "end": v(108.75, 87.5) * mm});
            skLineSegment(sketch, "E12.40.0.0", {"start": v(116.25, 87.5) * mm, "end": v(116.25, -87.5) * mm});
            skLineSegment(sketch, "E12.40.0.1", {"start": v(116.75, 87.5) * mm, "end": v(116.75, -87.5) * mm});
            skLineSegment(sketch, "E12.40.0.2", {"start": v(116.25, -87.5) * mm, "end": v(116.75, -87.5) * mm});
            skLineSegment(sketch, "E12.40.0.3", {"start": v(116.25, 87.5) * mm, "end": v(116.75, 87.5) * mm});
            skLineSegment(sketch, "E12.41.0.0", {"start": v(124.25, 87.5) * mm, "end": v(124.25, -87.5) * mm});
            skLineSegment(sketch, "E12.41.0.1", {"start": v(124.75, 87.5) * mm, "end": v(124.75, -87.5) * mm});
            skLineSegment(sketch, "E12.41.0.2", {"start": v(124.25, -87.5) * mm, "end": v(124.75, -87.5) * mm});
            skLineSegment(sketch, "E12.41.0.3", {"start": v(124.25, 87.5) * mm, "end": v(124.75, 87.5) * mm});
            skLineSegment(sketch, "E12.42.0.0", {"start": v(132.25, 87.5) * mm, "end": v(132.25, -87.5) * mm});
            skLineSegment(sketch, "E12.42.0.1", {"start": v(132.75, 87.5) * mm, "end": v(132.75, -87.5) * mm});
            skLineSegment(sketch, "E12.42.0.2", {"start": v(132.25, -87.5) * mm, "end": v(132.75, -87.5) * mm});
            skLineSegment(sketch, "E12.42.0.3", {"start": v(132.25, 87.5) * mm, "end": v(132.75, 87.5) * mm});
            skLineSegment(sketch, "E12.43.0.0", {"start": v(140.25, 87.5) * mm, "end": v(140.25, -87.5) * mm});
            skLineSegment(sketch, "E12.43.0.1", {"start": v(140.75, 87.5) * mm, "end": v(140.75, -87.5) * mm});
            skLineSegment(sketch, "E12.43.0.2", {"start": v(140.25, -87.5) * mm, "end": v(140.75, -87.5) * mm});
            skLineSegment(sketch, "E12.43.0.3", {"start": v(140.25, 87.5) * mm, "end": v(140.75, 87.5) * mm});
            skLineSegment(sketch, "E12.44.0.0", {"start": v(148.25, 87.5) * mm, "end": v(148.25, -87.5) * mm});
            skLineSegment(sketch, "E12.44.0.1", {"start": v(148.75, 87.5) * mm, "end": v(148.75, -87.5) * mm});
            skLineSegment(sketch, "E12.44.0.2", {"start": v(148.25, -87.5) * mm, "end": v(148.75, -87.5) * mm});
            skLineSegment(sketch, "E12.44.0.3", {"start": v(148.25, 87.5) * mm, "end": v(148.75, 87.5) * mm});
            skLineSegment(sketch, "E12.45.0.0", {"start": v(156.25, 87.5) * mm, "end": v(156.25, -87.5) * mm});
            skLineSegment(sketch, "E12.45.0.1", {"start": v(156.75, 87.5) * mm, "end": v(156.75, -87.5) * mm});
            skLineSegment(sketch, "E12.45.0.2", {"start": v(156.25, -87.5) * mm, "end": v(156.75, -87.5) * mm});
            skLineSegment(sketch, "E12.45.0.3", {"start": v(156.25, 87.5) * mm, "end": v(156.75, 87.5) * mm});
            skLineSegment(sketch, "E12.46.0.0", {"start": v(164.25, 87.5) * mm, "end": v(164.25, -87.5) * mm});
            skLineSegment(sketch, "E12.46.0.1", {"start": v(164.75, 87.5) * mm, "end": v(164.75, -87.5) * mm});
            skLineSegment(sketch, "E12.46.0.2", {"start": v(164.25, -87.5) * mm, "end": v(164.75, -87.5) * mm});
            skLineSegment(sketch, "E12.46.0.3", {"start": v(164.25, 87.5) * mm, "end": v(164.75, 87.5) * mm});
            skLineSegment(sketch, "E12.47.0.0", {"start": v(172.25, 87.5) * mm, "end": v(172.25, -87.5) * mm});
            skLineSegment(sketch, "E12.47.0.1", {"start": v(172.75, 87.5) * mm, "end": v(172.75, -87.5) * mm});
            skLineSegment(sketch, "E12.47.0.2", {"start": v(172.25, -87.5) * mm, "end": v(172.75, -87.5) * mm});
            skLineSegment(sketch, "E12.47.0.3", {"start": v(172.25, 87.5) * mm, "end": v(172.75, 87.5) * mm});
            skLineSegment(sketch, "E12.48.0.0", {"start": v(180.25, 87.5) * mm, "end": v(180.25, -87.5) * mm});
            skLineSegment(sketch, "E12.48.0.1", {"start": v(180.75, 87.5) * mm, "end": v(180.75, -87.5) * mm});
            skLineSegment(sketch, "E12.48.0.2", {"start": v(180.25, -87.5) * mm, "end": v(180.75, -87.5) * mm});
            skLineSegment(sketch, "E12.48.0.3", {"start": v(180.25, 87.5) * mm, "end": v(180.75, 87.5) * mm});
            skLineSegment(sketch, "E12.49.0.0", {"start": v(188.25, 87.5) * mm, "end": v(188.25, -87.5) * mm});
            skLineSegment(sketch, "E12.49.0.1", {"start": v(188.75, 87.5) * mm, "end": v(188.75, -87.5) * mm});
            skLineSegment(sketch, "E12.49.0.2", {"start": v(188.25, -87.5) * mm, "end": v(188.75, -87.5) * mm});
            skLineSegment(sketch, "E12.49.0.3", {"start": v(188.25, 87.5) * mm, "end": v(188.75, 87.5) * mm});
            skLineSegment(sketch, "E12.50.0.0", {"start": v(196.25, 87.5) * mm, "end": v(196.25, -87.5) * mm});
            skLineSegment(sketch, "E12.50.0.1", {"start": v(196.75, 87.5) * mm, "end": v(196.75, -87.5) * mm});
            skLineSegment(sketch, "E12.50.0.2", {"start": v(196.25, -87.5) * mm, "end": v(196.75, -87.5) * mm});
            skLineSegment(sketch, "E12.50.0.3", {"start": v(196.25, 87.5) * mm, "end": v(196.75, 87.5) * mm});
            skLineSegment(sketch, "E12.direction1", {"start": v(-203.75, -87.5) * mm, "end": v(-195.75, -87.5) * mm, "construction": true});
            skSolve(sketch);
        }
        {
            var Q0;
            Q0 = qSketchRegion(id + "F12", true);
            extrude(context, id + "F13", {"entities" : qUnion([Q0]), "depth" : -1 * mm, "offsetDistance" : 25 * mm});
        }
        {
            var Q0;
            Q0=makeQuery(id+"F9.opExtrude","CAP_FACE",FACE,{"disambiguationData":[OSD([sQuery(id+"F8.wireOp",EDGE,"E7.bottom"),sQuery(id+"F8.wireOp",EDGE,"E7.top"),sQuery(id+"F8.wireOp",EDGE,"E7.left"),sQuery(id+"F8.wireOp",EDGE,"E7.right"),sQuery(id+"F8.wireOp",EDGE,"E8.bottom"),sQuery(id+"F8.wireOp",EDGE,"E8.top"),sQuery(id+"F8.wireOp",EDGE,"E8.left"),sQuery(id+"F8.wireOp",EDGE,"E8.right")])],"isStart":true});
            var sketch = newSketch(context, id + "F14", { "sketchPlane" : qUnion([Q0])});
            skCircle(sketch, "E13", {"center": v(0, 0) * mm, "radius": 37.5 * mm});
            skSolve(sketch);
        }
        {
            var Q0;
            Q0 = qSketchRegion(id + "F14", true);
            extrude(context, id + "F15", {"entities" : qUnion([Q0]), "depth" : 25 * mm, "offsetDistance" : 25 * mm});
        }
        {
            var Q0;
            Q0=makeQuery(id+"F15.opExtrude","CAP_FACE",FACE,{"disambiguationData":[OSD([sQuery(id+"F14.wireOp",EDGE,"E13")])],"isStart":false});
            var sketch = newSketch(context, id + "F16", { "sketchPlane" : qUnion([Q0])});
            skCircle(sketch, "E14", {"center": v(0, 0) * mm, "radius": 45 * mm});
            skSolve(sketch);
        }
        {
            var Q0;
            Q0 = qSketchRegion(id + "F16", true);
            var Q1;
            Q1 = qConstructionFilter(qBodyType(qCreatedBy(id + "F16" ,EDGE), BodyType.WIRE), ConstructionObject.NO);
            extrude(context, id + "F17", {"entities" : qUnion([Q0]), "operationType" : NewBodyOperationType.ADD, "surfaceEntities" : qUnion([Q1]), "depth" : 155 * mm, "offsetDistance" : 25 * mm});
        }
        {
            var Q0;
            Q0=makeQuery(id+"F15.opExtrude","CAP_EDGE",EDGE,{"disambiguationData":[OSD([sQuery(id+"F14.wireOp",EDGE,"E13")])],"isStart":true});
            var Q1;
            Q1=makeQuery(id+"F17.opExtrude","CAP_EDGE",EDGE,{"disambiguationData":[OSD([sQuery(id+"F16.wireOp",EDGE,"E14")])],"isStart":false});
            var Q2;
            Q2=makeQuery(id+"F15.opExtrude","CAP_EDGE",EDGE,{"disambiguationData":[OSD([sQuery(id+"F14.wireOp",EDGE,"E13")])],"isStart":false});
            fillet(context, id + "F18", {"entities" : qUnion([Q0, Q1, Q2]), "radius" : 5 * mm, "tangentPropagation" : true, "allowEdgeOverflow" : false});
        }
        {
            var Q0;
            Q0=makeQuery(id+"F17.opExtrude","CAP_EDGE",EDGE,{"disambiguationData":[OSD([sQuery(id+"F16.wireOp",EDGE,"E14")])],"isStart":true});
            fillet(context, id + "F19", {"entities" : qUnion([Q0]), "radius" : 5 * mm, "tangentPropagation" : true, "allowEdgeOverflow" : false});
        }
        {
            var Q0;
            Q0=makeQuery(id+"F17.opExtrude","CAP_FACE",FACE,{"disambiguationData":[OSD([sQuery(id+"F16.wireOp",EDGE,"E14")])],"isStart":false});
            var sketch = newSketch(context, id + "F20", { "sketchPlane" : qUnion([Q0])});
            skLineSegment(sketch, "E15.bottom", {"start": v(50, 50) * mm, "end": v(-50, 50) * mm});
            skLineSegment(sketch, "E15.top", {"start": v(50, -50) * mm, "end": v(-50, -50) * mm});
            skLineSegment(sketch, "E15.left", {"start": v(50, 50) * mm, "end": v(50, -50) * mm});
            skLineSegment(sketch, "E15.right", {"start": v(-50, 50) * mm, "end": v(-50, -50) * mm});
            skPoint(sketch, "E15.middle", {"position": v(0, 0) * mm});
            skSolve(sketch);
        }
        {
            var Q0;
            Q0 = qSketchRegion(id + "F20", true);
            extrude(context, id + "F21", {"entities" : qUnion([Q0]), "operationType" : NewBodyOperationType.ADD, "depth" : 2.5 * mm, "offsetDistance" : 25 * mm});
        }
    });
